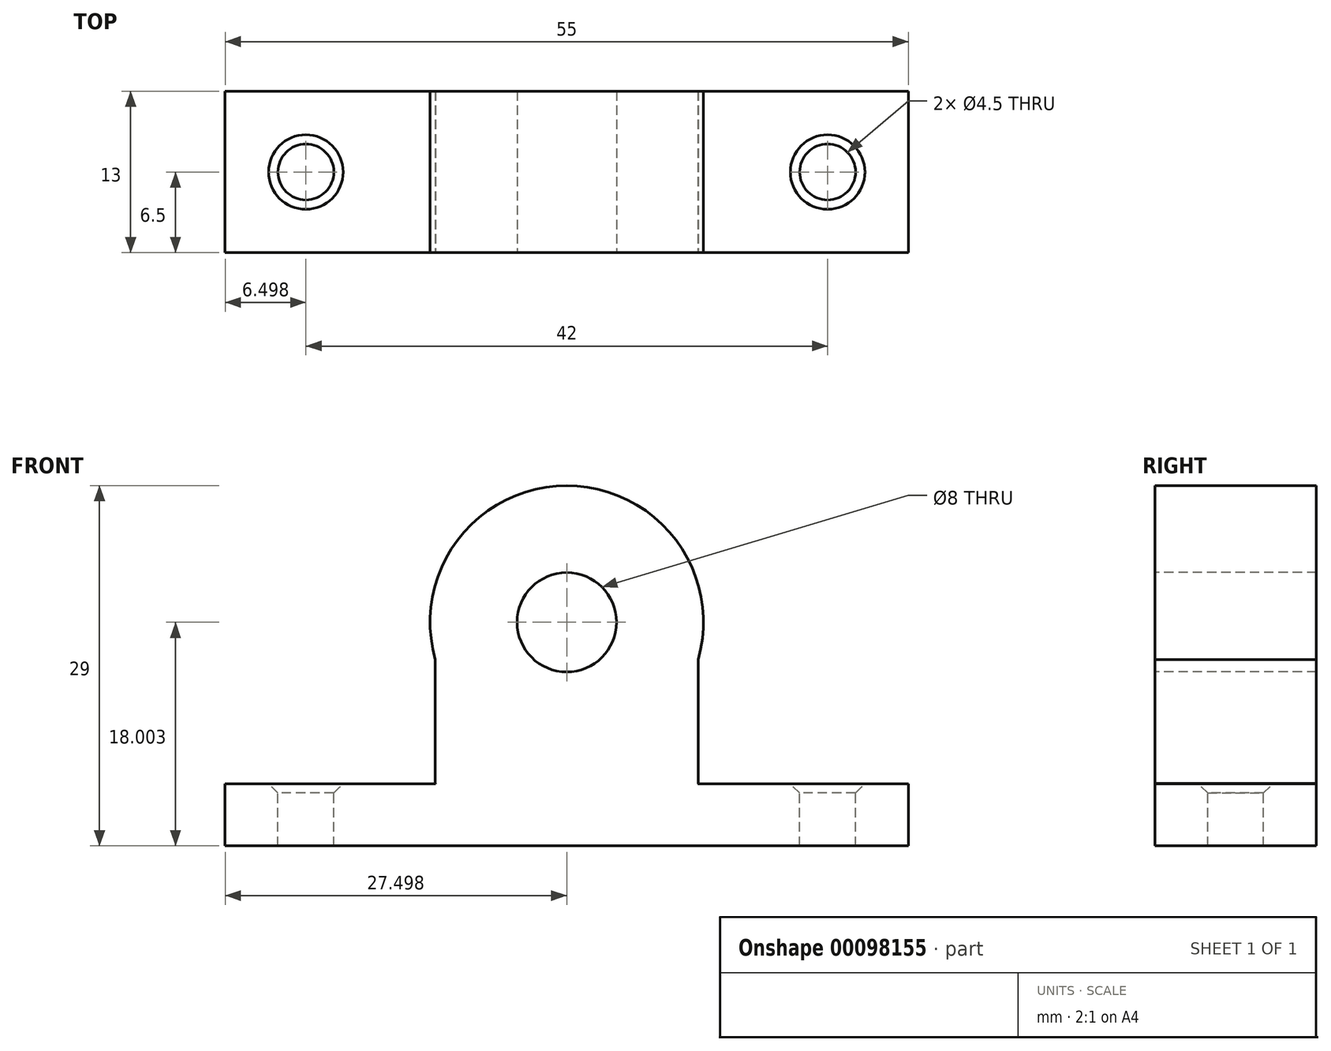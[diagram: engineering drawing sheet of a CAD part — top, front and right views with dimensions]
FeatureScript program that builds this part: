
annotation { "Feature Type Name" : "Feature", "Feature Type Description" : "" }
export const myFeature = defineFeature(function(context is Context, id is Id, definition is map)
    precondition{}
    {
        {
            var Q0;
            Q0=qCreatedBy(makeId("Front.planeOp"),FACE);
            var sketch = newSketch(context, id + "F0", { "sketchPlane" : qUnion([Q0])});
            skCircle(sketch, "E0", {"center": v(-34.47, 44.6) * mm, "radius": 4 * mm});
            skLineSegment(sketch, "E1", {"start": v(-61.97, 26.6) * mm, "end": v(-6.97, 26.6) * mm});
            skLineSegment(sketch, "E2", {"start": v(-61.97, 26.6) * mm, "end": v(-61.97, 31.6) * mm});
            skLineSegment(sketch, "E3", {"start": v(-6.97, 26.6) * mm, "end": v(-6.97, 31.6) * mm});
            skArc(sketch, "E4", {"start": v(-23.89, 41.6) * mm, "mid": v(-34.47, 55.6) * mm, "end": v(-45.06, 41.6) * mm});
            skLineSegment(sketch, "E5", {"start": v(-61.97, 31.6) * mm, "end": v(-45.03, 31.6) * mm});
            skLineSegment(sketch, "E6", {"start": v(-45.06, 41.6) * mm, "end": v(-45.06, 31.6) * mm});
            skLineSegment(sketch, "E7", {"start": v(-23.89, 41.6) * mm, "end": v(-23.89, 31.6) * mm});
            skArc(sketch, "E8", {"start": v(-45.06, 31.62) * mm, "mid": v(-45.05, 31.61) * mm, "end": v(-45.03, 31.6) * mm});
            skLineSegment(sketch, "E9.trimOffspring", {"start": v(-23.91, 31.6) * mm, "end": v(-6.97, 31.6) * mm});
            skArc(sketch, "E10.trimOffspring", {"start": v(-23.91, 31.6) * mm, "mid": v(-23.9, 31.61) * mm, "end": v(-23.89, 31.62) * mm});
            skSolve(sketch);
        }
        {
            var Q0;
            Q0=makeQuery(id+"F0.imprint","IMPRINT",FACE,{"disambiguationData":[TD([[makeQuery(id+"F0.imprint","IMPRINT",EDGE,{"derivedFrom":sQuery(id+"F0.wireOp",EDGE,"E0")}),-1.0]])]});
            extrude(context, id + "F1", {"entities" : qUnion([Q0]), "oppositeDirection" : true, "depth" : 13 * mm});
        }
        {
            var Q0;
            Q0=makeQuery(id+"F1.opExtrude","SWEPT_FACE",FACE,{"disambiguationData":[OSD([sQuery(id+"F0.wireOp",EDGE,"E5")])]});
            var sketch = newSketch(context, id + "F2", { "sketchPlane" : qUnion([Q0])});
            skPoint(sketch, "E11", {"position": v(-55.47, 6.5) * mm});
            skLineSegment(sketch, "E12", {"start": v(-34.47, 30.74) * mm, "end": v(-34.47, -16.7) * mm, "construction": true});
            skPoint(sketch, "E13.MirrorP", {"position": v(-13.47, 6.5) * mm});
            skSolve(sketch);
        }
        {
            var Q0;
            Q0=sQuery(id+"F2.wireOp",VERTEX,"E11");
            var Q1;
            Q1=sQuery(id+"F2.wireOp",VERTEX,"E13.MirrorP");
            var Q2;
            Q2=makeQuery(id+"F1.opExtrude","SWEPT_BODY",BODY,{"disambiguationData":[OSD([sQuery(id+"F0.wireOp",EDGE,"E0"),sQuery(id+"F0.wireOp",EDGE,"E1"),sQuery(id+"F0.wireOp",EDGE,"E2"),sQuery(id+"F0.wireOp",EDGE,"E3"),sQuery(id+"F0.wireOp",EDGE,"E4"),sQuery(id+"F0.wireOp",EDGE,"E5"),sQuery(id+"F0.wireOp",EDGE,"E6"),sQuery(id+"F0.wireOp",EDGE,"E7"),sQuery(id+"F0.wireOp",EDGE,"E8"),sQuery(id+"F0.wireOp",EDGE,"E9.trimOffspring"),sQuery(id+"F0.wireOp",EDGE,"E10.trimOffspring")])]});
            hole(context, id + "F3", {"style" : HoleStyle.C_SINK, "endStyle" : HoleEndStyle.BLIND, "holeDiameter" : 4.5 * mm, "cSinkDiameter" : 6 * mm, "cSinkAngle" : 90 * degree, "holeDepth" : 5 * mm, "locations" : qUnion([Q0, Q1]), "scope" : qUnion([Q2])});
        }
    });
